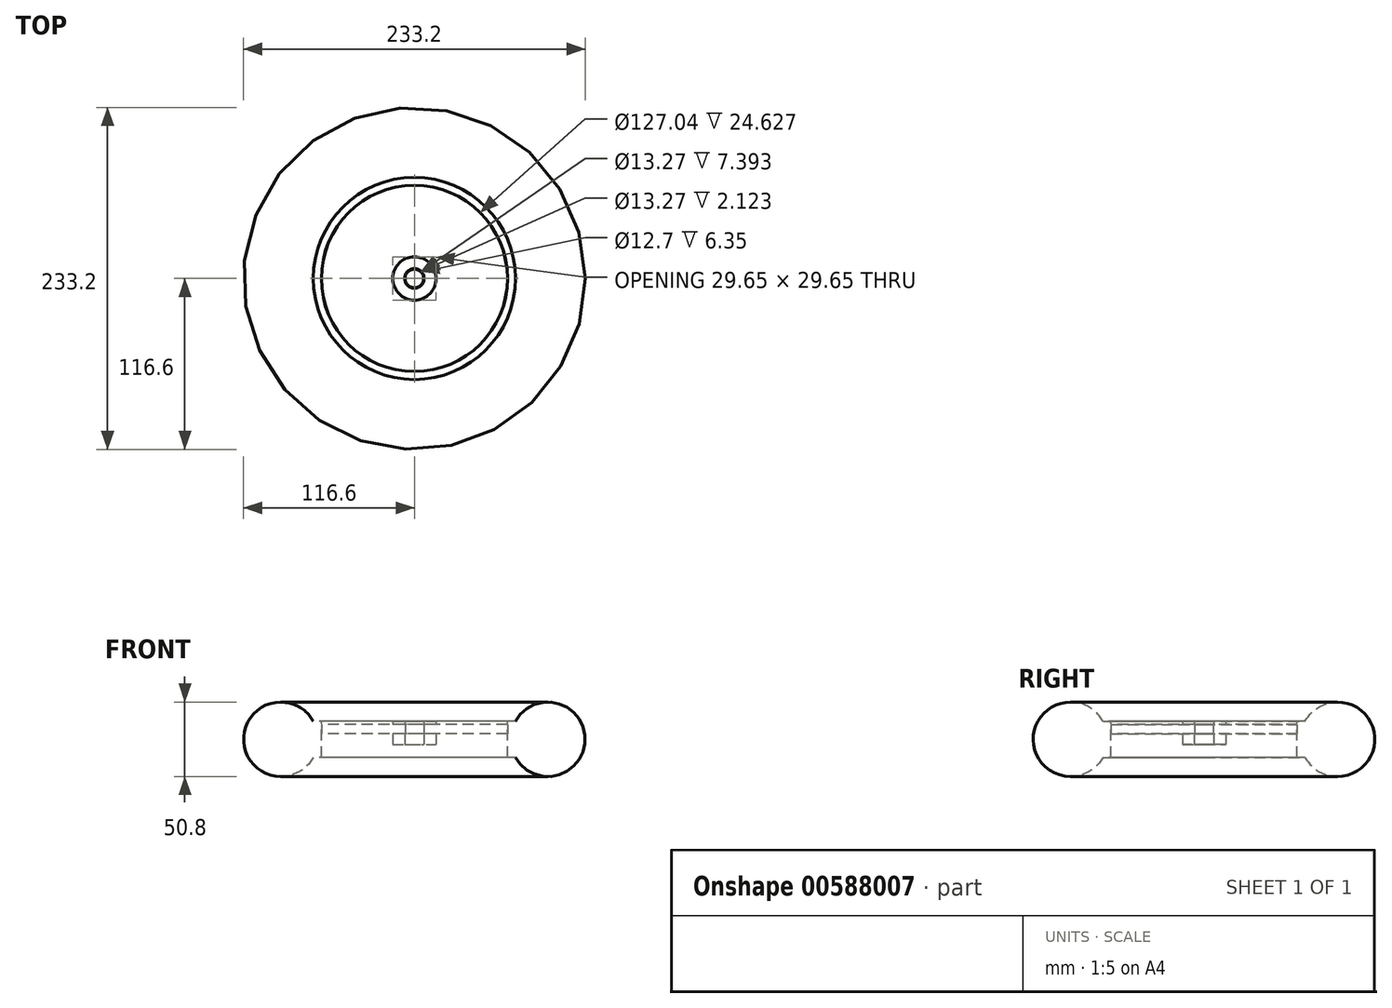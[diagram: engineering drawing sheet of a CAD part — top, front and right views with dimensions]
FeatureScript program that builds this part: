
annotation { "Feature Type Name" : "Feature", "Feature Type Description" : "" }
export const myFeature = defineFeature(function(context is Context, id is Id, definition is map)
    precondition{}
    {
        {
            var Q0;
            Q0=qCreatedBy(makeId("Top.planeOp"),FACE);
            var sketch = newSketch(context, id + "F0", { "sketchPlane" : qUnion([Q0])});
            skCircle(sketch, "E0", {"center": v(0, 0) * mm, "radius": 63.5 * mm});
            skCircle(sketch, "E1", {"center": v(0, 0) * mm, "radius": 6.35 * mm});
            skSolve(sketch);
        }
        {
            var Q0;
            Q0=makeQuery(id+"F0.imprint","IMPRINT",FACE,{"disambiguationData":[TD([[makeQuery(id+"F0.imprint","IMPRINT",EDGE,{"derivedFrom":sQuery(id+"F0.wireOp",EDGE,"E0")}),1.0]])]});
            extrude(context, id + "F1", {"entities" : qUnion([Q0]), "depth" : 6.35 * mm, "offsetDistance" : 25.4 * mm});
        }
        {
            var Q0;
            Q0=qCreatedBy(makeId("Right.planeOp"),FACE);
            var sketch = newSketch(context, id + "F2", { "sketchPlane" : qUnion([Q0])});
            skCircle(sketch, "E2", {"center": v(-91.2, -3.86) * mm, "radius": 25.4 * mm});
            skLineSegment(sketch, "E3.bottom", {"start": v(-63.52, -16.17) * mm, "end": v(-68.98, -16.17) * mm});
            skLineSegment(sketch, "E3.top", {"start": v(-63.52, 8.45) * mm, "end": v(-68.98, 8.45) * mm});
            skLineSegment(sketch, "E3.left", {"start": v(-63.52, -16.17) * mm, "end": v(-63.52, 8.45) * mm});
            skLineSegment(sketch, "E3.right", {"start": v(-68.98, -16.17) * mm, "end": v(-68.98, 8.45) * mm});
            skSolve(sketch);
        }
        {
            var Q0;
            {var subQ0=sQuery(id+"F2.wireOp",EDGE,"E3.right");Q0=makeQuery(id+"F2.imprint","IMPRINT",FACE,{"disambiguationData":[TD([[makeQuery(id+"F2.imprint","IMPRINT",EDGE,{"derivedFrom":subQ0}),-1.0]])]});}
            var Q1;
            {var subQ0=sQuery(id+"F2.wireOp",EDGE,"E3.right");Q1=makeQuery(id+"F2.imprint","IMPRINT",FACE,{"disambiguationData":[TD([[makeQuery(id+"F2.imprint","IMPRINT",EDGE,{"derivedFrom":subQ0}),1.0]])]});}
            var Q2;
            {var subQ1=sQuery(id+"F2.wireOp",EDGE,"E3.bottom");Q2=makeQuery(id+"F2.imprint","IMPRINT",FACE,{"disambiguationData":[TD([[makeQuery(id+"F2.imprint","IMPRINT",EDGE,{"derivedFrom":subQ1}),-1.0]])]});}
            var Q3;
            Q3=makeQuery(id+"F1.opExtrude","SWEPT_FACE",FACE,{"disambiguationData":[OSD([sQuery(id+"F0.wireOp",EDGE,"E0")])]});
            revolve(context, id + "F3", {"entities" : qUnion([Q0, Q1, Q2]), "axis" : qUnion([Q3]), "revolveType" : RevolveType.FULL});
        }
        {
            var Q0;
            Q0=qCreatedBy(makeId("Right.planeOp"),FACE);
            var sketch = newSketch(context, id + "F4", { "sketchPlane" : qUnion([Q0])});
            skLineSegment(sketch, "E4.bottom", {"start": v(-14.82, 8.47) * mm, "end": v(-6.63, 8.47) * mm});
            skLineSegment(sketch, "E4.top", {"start": v(-14.82, -7.4) * mm, "end": v(-6.63, -7.4) * mm});
            skLineSegment(sketch, "E4.left", {"start": v(-14.82, 8.47) * mm, "end": v(-14.82, -7.4) * mm});
            skLineSegment(sketch, "E4.right", {"start": v(-6.63, 8.47) * mm, "end": v(-6.63, -7.4) * mm});
            skSolve(sketch);
        }
        {
            var Q0;
            Q0 = qSketchRegion(id + "F4", true);
            var Q1;
            Q1=makeQuery(id+"F1.opExtrude","CAP_EDGE",EDGE,{"disambiguationData":[OSD([sQuery(id+"F0.wireOp",EDGE,"E0")])],"isStart":false});
            revolve(context, id + "F5", {"operationType" : NewBodyOperationType.ADD, "entities" : qUnion([Q0]), "axis" : qUnion([Q1]), "revolveType" : RevolveType.FULL});
        }
    });
